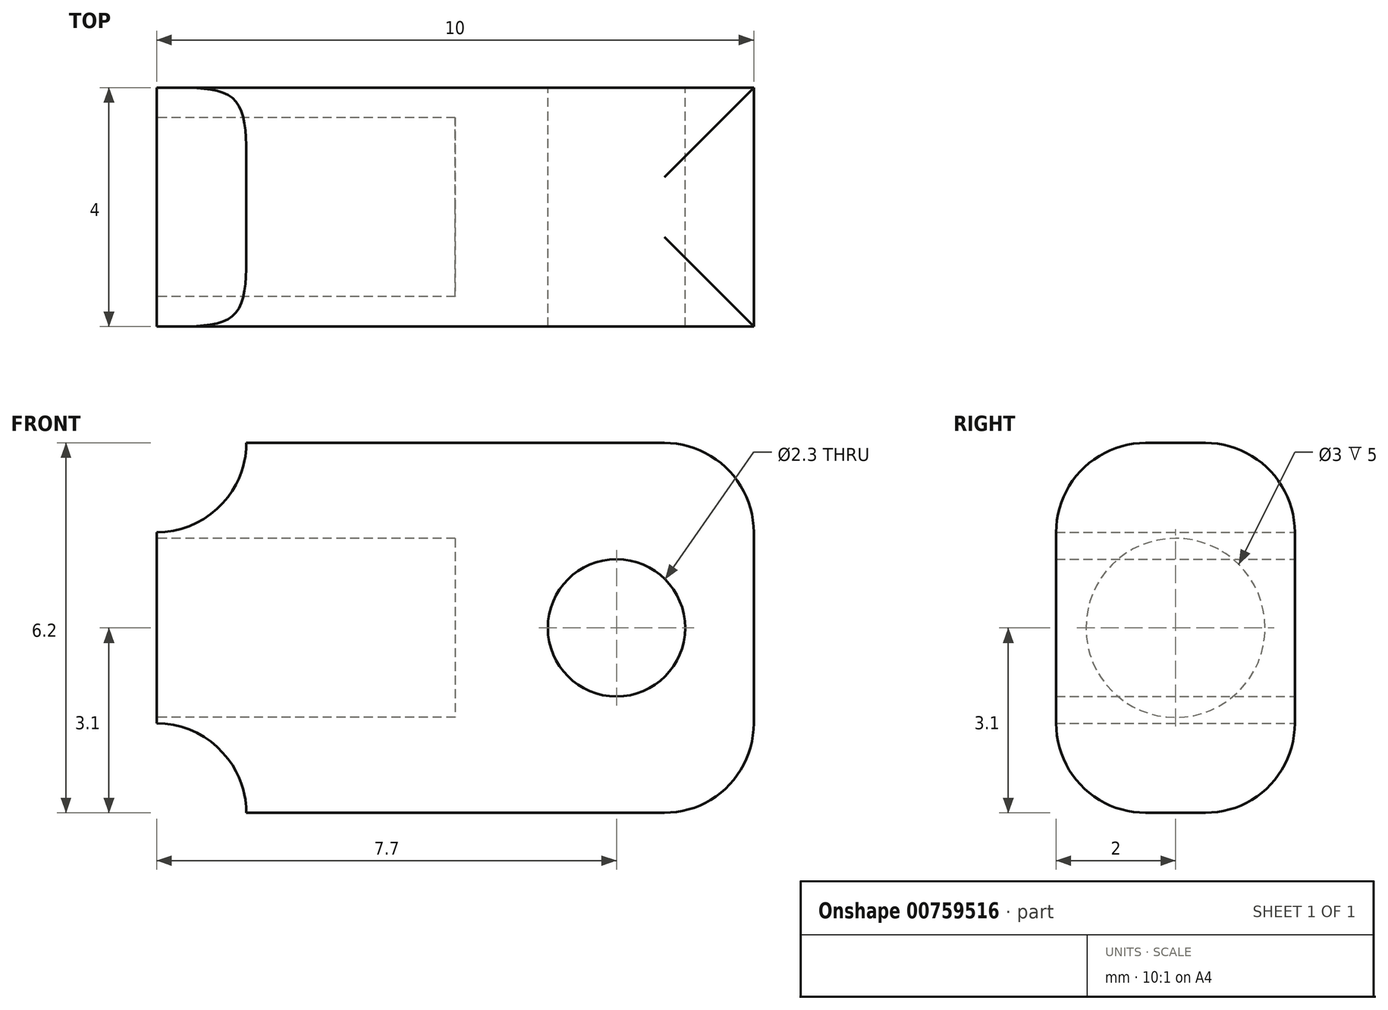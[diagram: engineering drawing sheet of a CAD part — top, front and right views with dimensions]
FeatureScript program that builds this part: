
annotation { "Feature Type Name" : "Feature", "Feature Type Description" : "" }
export const myFeature = defineFeature(function(context is Context, id is Id, definition is map)
    precondition{}
    {
        {
            var Q0;
            Q0=qCreatedBy(makeId("Front.planeOp"),FACE);
            var sketch = newSketch(context, id + "F0", { "sketchPlane" : qUnion([Q0])});
            skLineSegment(sketch, "E0.bottom", {"start": v(-3.5, 3.1) * mm, "end": v(5, 3.1) * mm});
            skLineSegment(sketch, "E0.top", {"start": v(-3.5, -3.1) * mm, "end": v(5, -3.1) * mm});
            skLineSegment(sketch, "E0.left", {"start": v(-5, 1.6) * mm, "end": v(-5, -1.6) * mm});
            skLineSegment(sketch, "E0.right", {"start": v(5, 3.1) * mm, "end": v(5, -3.1) * mm});
            skPoint(sketch, "E0.middle", {"position": v(0, 0) * mm});
            skArc(sketch, "E1", {"start": v(-5, 1.6) * mm, "mid": v(-3.94, 2.04) * mm, "end": v(-3.5, 3.1) * mm});
            skArc(sketch, "E2.MirrorCS", {"start": v(-5, -1.6) * mm, "mid": v(-3.94, -2.04) * mm, "end": v(-3.5, -3.1) * mm});
            skCircle(sketch, "E3", {"center": v(2.7, 0) * mm, "radius": 1.15 * mm});
            skSolve(sketch);
        }
        {
            var Q0;
            Q0 = qSketchRegion(id + "F0", true);
            extrude(context, id + "F1", {"entities" : qUnion([Q0]), "depth" : 4 * mm, "offsetDistance" : 25 * mm});
        }
        {
            var Q0;
            Q0=makeQuery(id+"F1.opExtrude","SWEPT_FACE",FACE,{"disambiguationData":[OSD([sQuery(id+"F0.wireOp",EDGE,"E0.left")])]});
            var sketch = newSketch(context, id + "F2", { "sketchPlane" : qUnion([Q0])});
            skCircle(sketch, "E4", {"center": v(2, 0) * mm, "radius": 1.5 * mm});
            skPoint(sketch, "E4.centerSnap0", {"position": v(2, 1.6) * mm});
            skSolve(sketch);
        }
        {
            var Q0;
            Q0 = qSketchRegion(id + "F2", true);
            extrude(context, id + "F3", {"entities" : qUnion([Q0]), "operationType" : NewBodyOperationType.REMOVE, "oppositeDirection" : true, "depth" : 5 * mm, "offsetDistance" : 25 * mm});
        }
        {
            var Q0;
            Q0=makeQuery(id+"F1.opExtrude","CAP_EDGE",EDGE,{"disambiguationData":[OSD([sQuery(id+"F0.wireOp",EDGE,"E0.bottom")])],"isStart":false});
            var Q1;
            Q1=makeQuery(id+"F1.opExtrude","CAP_EDGE",EDGE,{"disambiguationData":[OSD([sQuery(id+"F0.wireOp",EDGE,"E0.bottom")])],"isStart":true});
            var Q2;
            Q2=makeQuery(id+"F1.opExtrude","SWEPT_EDGE",EDGE,{"disambiguationData":[OSD([sQuery(id+"F0.wireOp",EDGE,"E0.bottom"),sQuery(id+"F0.wireOp",EDGE,"E0.right")])]});
            var Q3;
            Q3=makeQuery(id+"F1.opExtrude","CAP_EDGE",EDGE,{"disambiguationData":[OSD([sQuery(id+"F0.wireOp",EDGE,"E0.top")])],"isStart":true});
            var Q4;
            Q4=makeQuery(id+"F1.opExtrude","CAP_EDGE",EDGE,{"disambiguationData":[OSD([sQuery(id+"F0.wireOp",EDGE,"E0.top")])],"isStart":false});
            var Q5;
            Q5=makeQuery(id+"F1.opExtrude","SWEPT_EDGE",EDGE,{"disambiguationData":[OSD([sQuery(id+"F0.wireOp",EDGE,"E0.top"),sQuery(id+"F0.wireOp",EDGE,"E0.right")])]});
            fillet(context, id + "F4", {"entities" : qUnion([Q0, Q1, Q2, Q3, Q4, Q5]), "radius" : 1.5 * mm, "tangentPropagation" : true, "allowEdgeOverflow" : false});
        }
    });
